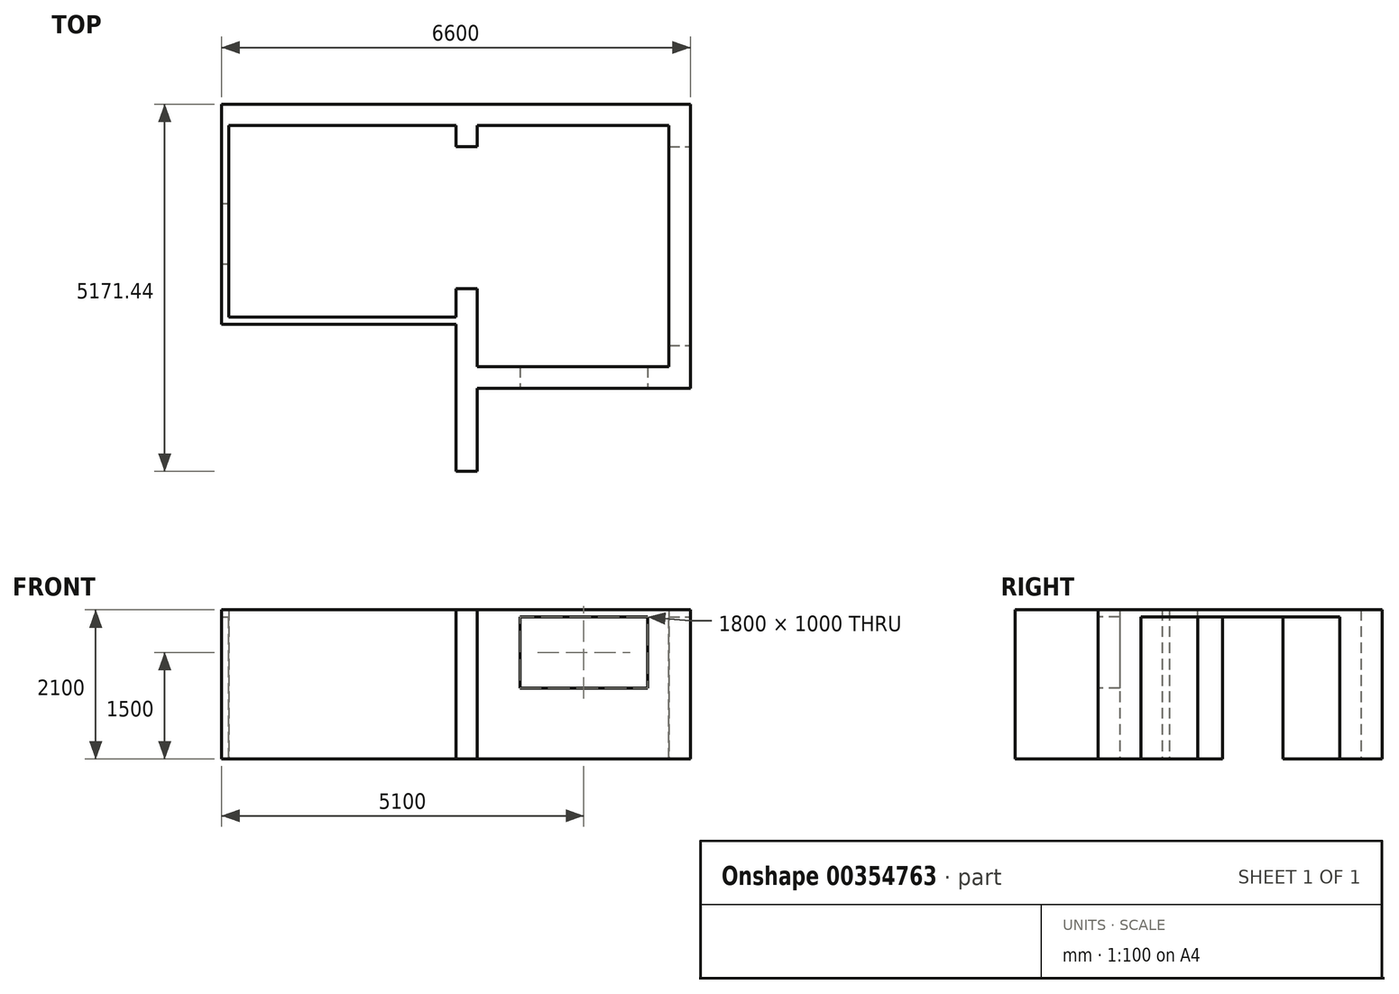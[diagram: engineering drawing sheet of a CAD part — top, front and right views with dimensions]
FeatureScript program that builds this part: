
annotation { "Feature Type Name" : "Feature", "Feature Type Description" : "" }
export const myFeature = defineFeature(function(context is Context, id is Id, definition is map)
    precondition{}
    {
        {
            var Q0;
            Q0=qCreatedBy(makeId("Top.planeOp"),FACE);
            var sketch = newSketch(context, id + "F0", { "sketchPlane" : qUnion([Q0])});
            skLineSegment(sketch, "E0.bottom", {"start": v(-1890.6, 1415.86) * mm, "end": v(1709.4, 1415.86) * mm});
            skLineSegment(sketch, "E0.top", {"start": v(-1890.6, -1684.14) * mm, "end": v(1709.4, -1684.14) * mm});
            skLineSegment(sketch, "E0.left", {"start": v(-1890.6, 1415.86) * mm, "end": v(-1890.6, -1684.14) * mm});
            skLineSegment(sketch, "E0.right", {"start": v(1709.4, 1415.86) * mm, "end": v(1709.4, -1684.14) * mm});
            skLineSegment(sketch, "E1.bottom", {"start": v(-1790.6, 1115.86) * mm, "end": v(1409.4, 1115.86) * mm});
            skLineSegment(sketch, "E1.top", {"start": v(-1790.6, -1584.14) * mm, "end": v(1409.4, -1584.14) * mm});
            skLineSegment(sketch, "E1.left", {"start": v(-1790.6, 1115.86) * mm, "end": v(-1790.6, -1584.14) * mm});
            skLineSegment(sketch, "E1.right", {"start": v(1409.4, 1115.86) * mm, "end": v(1409.4, -1584.14) * mm});
            skLineSegment(sketch, "E2.bottom", {"start": v(1709.4, 1415.86) * mm, "end": v(4709.4, 1415.86) * mm});
            skLineSegment(sketch, "E2.top", {"start": v(1709.4, -2584.14) * mm, "end": v(4709.4, -2584.14) * mm});
            skLineSegment(sketch, "E2.left", {"start": v(1709.4, 1415.86) * mm, "end": v(1709.4, -2584.14) * mm});
            skLineSegment(sketch, "E2.right", {"start": v(4709.4, 1415.86) * mm, "end": v(4709.4, -2584.14) * mm});
            skLineSegment(sketch, "E3", {"start": v(1709.4, 1115.86) * mm, "end": v(4409.4, 1115.86) * mm});
            skLineSegment(sketch, "E4", {"start": v(4409.4, 1115.86) * mm, "end": v(4409.4, -2284.14) * mm});
            skLineSegment(sketch, "E5", {"start": v(4409.4, -2284.14) * mm, "end": v(1709.4, -2284.14) * mm});
            skLineSegment(sketch, "E6.bottom", {"start": v(1409.4, -1684.14) * mm, "end": v(1709.4, -1684.14) * mm});
            skLineSegment(sketch, "E6.top", {"start": v(1409.4, -3755.58) * mm, "end": v(1709.4, -3755.58) * mm});
            skLineSegment(sketch, "E6.left", {"start": v(1409.4, -1684.14) * mm, "end": v(1409.4, -3755.58) * mm});
            skLineSegment(sketch, "E6.right", {"start": v(1709.4, -1684.14) * mm, "end": v(1709.4, -3755.58) * mm});
            skSolve(sketch);
        }
        {
            var Q0;
            Q0=qSketchRegion(id+"F0",true);
            extrude(context, id + "F1", {"entities" : qUnion([Q0]), "depth" : 2100 * mm});
        }
        {
            var Q0;
            Q0=makeQuery(id+"F1.opExtrude","CAP_FACE",FACE,{"disambiguationData":[OSD([sQuery(id+"F0.wireOp",EDGE,"E0.bottom"),sQuery(id+"F0.wireOp",EDGE,"E0.top"),sQuery(id+"F0.wireOp",EDGE,"E0.left"),sQuery(id+"F0.wireOp",EDGE,"E1.bottom"),sQuery(id+"F0.wireOp",EDGE,"E1.top"),sQuery(id+"F0.wireOp",EDGE,"E1.left"),sQuery(id+"F0.wireOp",EDGE,"E1.right"),sQuery(id+"F0.wireOp",EDGE,"E2.bottom"),sQuery(id+"F0.wireOp",EDGE,"E2.top"),sQuery(id+"F0.wireOp",EDGE,"E2.left"),sQuery(id+"F0.wireOp",EDGE,"E2.right"),sQuery(id+"F0.wireOp",EDGE,"E3"),sQuery(id+"F0.wireOp",EDGE,"E4"),sQuery(id+"F0.wireOp",EDGE,"E5"),sQuery(id+"F0.wireOp",EDGE,"E6.top"),sQuery(id+"F0.wireOp",EDGE,"E6.left"),sQuery(id+"F0.wireOp",EDGE,"E6.right")])],"isStart":false});
            var sketch = newSketch(context, id + "F2", { "sketchPlane" : qUnion([Q0])});
            skLineSegment(sketch, "E7.bottom", {"start": v(1409.4, -1184.14) * mm, "end": v(1709.4, -1184.14) * mm});
            skLineSegment(sketch, "E7.top", {"start": v(1409.4, 815.86) * mm, "end": v(1709.4, 815.86) * mm});
            skLineSegment(sketch, "E7.left", {"start": v(1409.4, -1184.14) * mm, "end": v(1409.4, 815.86) * mm});
            skLineSegment(sketch, "E7.right", {"start": v(1709.4, -1184.14) * mm, "end": v(1709.4, 815.86) * mm});
            skSolve(sketch);
        }
        {
            var Q0;
            Q0=qSketchRegion(id+"F2",true);
            extrude(context, id + "F3", {"entities" : qUnion([Q0]), "operationType" : NewBodyOperationType.REMOVE, "oppositeDirection" : true, "depth" : 3450 * mm});
        }
        {
            var Q0;
            Q0=makeQuery(id+"F1.opExtrude","SWEPT_FACE",FACE,{"disambiguationData":[OSD([sQuery(id+"F0.wireOp",EDGE,"E2.right")])]});
            var sketch = newSketch(context, id + "F4", { "sketchPlane" : qUnion([Q0])});
            skLineSegment(sketch, "E8.bottom", {"start": v(-1984.14, 0) * mm, "end": v(815.86, 0) * mm});
            skLineSegment(sketch, "E8.top", {"start": v(-1984.14, 2000) * mm, "end": v(815.86, 2000) * mm});
            skLineSegment(sketch, "E8.left", {"start": v(-1984.14, 0) * mm, "end": v(-1984.14, 2000) * mm});
            skLineSegment(sketch, "E8.right", {"start": v(815.86, 0) * mm, "end": v(815.86, 2000) * mm});
            skSolve(sketch);
        }
        {
            var Q0;
            Q0=qSketchRegion(id+"F4",true);
            extrude(context, id + "F5", {"entities" : qUnion([Q0]), "operationType" : NewBodyOperationType.REMOVE, "oppositeDirection" : true, "depth" : 880 * mm});
        }
        {
            var Q0;
            Q0=makeQuery(id+"F1.opExtrude","SWEPT_FACE",FACE,{"disambiguationData":[OSD([sQuery(id+"F0.wireOp",EDGE,"E2.top")])]});
            var sketch = newSketch(context, id + "F6", { "sketchPlane" : qUnion([Q0])});
            skLineSegment(sketch, "E9.bottom", {"start": v(2309.4, 2000) * mm, "end": v(4109.4, 2000) * mm});
            skLineSegment(sketch, "E9.top", {"start": v(2309.4, 1000) * mm, "end": v(4109.4, 1000) * mm});
            skLineSegment(sketch, "E9.left", {"start": v(2309.4, 2000) * mm, "end": v(2309.4, 1000) * mm});
            skLineSegment(sketch, "E9.right", {"start": v(4109.4, 2000) * mm, "end": v(4109.4, 1000) * mm});
            skSolve(sketch);
        }
        {
            var Q0;
            Q0=qSketchRegion(id+"F6",true);
            extrude(context, id + "F7", {"entities" : qUnion([Q0]), "operationType" : NewBodyOperationType.REMOVE, "oppositeDirection" : true, "depth" : 700 * mm});
        }
        {
            var Q0;
            Q0=makeQuery(id+"F1.opExtrude","SWEPT_FACE",FACE,{"disambiguationData":[OSD([sQuery(id+"F0.wireOp",EDGE,"E1.left")])]});
            var sketch = newSketch(context, id + "F8", { "sketchPlane" : qUnion([Q0])});
            skPoint(sketch, "E10.oppositeSnap0", {"position": v(15.86, 2100) * mm});
            skLineSegment(sketch, "E10.bottom", {"start": v(-834.14, 0) * mm, "end": v(15.86, 0) * mm});
            skLineSegment(sketch, "E10.top", {"start": v(-834.14, 2000) * mm, "end": v(15.86, 2000) * mm});
            skLineSegment(sketch, "E10.left", {"start": v(-834.14, 0) * mm, "end": v(-834.14, 2000) * mm});
            skLineSegment(sketch, "E10.right", {"start": v(15.86, 0) * mm, "end": v(15.86, 2000) * mm});
            skSolve(sketch);
        }
        {
            var Q0;
            Q0=qSketchRegion(id+"F8",true);
            extrude(context, id + "F9", {"entities" : qUnion([Q0]), "operationType" : NewBodyOperationType.REMOVE, "oppositeDirection" : true, "depth" : 620 * mm});
        }
    });
